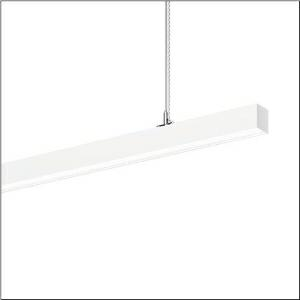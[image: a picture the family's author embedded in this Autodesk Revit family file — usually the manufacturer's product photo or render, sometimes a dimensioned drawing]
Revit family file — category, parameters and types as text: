
# Revit family: silica_r__21_51mx33tat7w_2751
name_source: partatom
category: Lighting Fixtures
units: mm (PartAtom-declared; Revit-internal decimal feet)

## family parameters
Cut with Voids When Loaded = No
Host = Face
Light Source = No
Part Type = Normal
Room Calculation Point = No
Round Connector Dimension = Use Diameter
Shared = No

## types (1)
- --- (1 x LED, 5740 lm, 53.8 W, 6500K)
    Apparent Load = 54 VA
    CIE Flux Codes = 78 96 99 56 100
    Color Rendering = 80
    Color Temperature = 6500K
    Default Elevation = 1800 mm
    Description = Silica® 21, office luminaire, primary optical cover: prismatic diffuser, of PMMA, CAT 2 (L<= 3000cd/m²), light emission: direct/indirect distribution, primary light characteristic: symmetric, installation type: suspended mounting, LED, rated luminous flux: 5.740lm, luminous efficacy: 102lm/W, light colour: 8tw, colour temperature: 2700..6500K, control gear: ECG DALI, with terminal, 3+2-pole, max. 2.5mm², mains connection: 220..240V, AC, 50/60Hz, rated input power: 56.5W, luminaire housing, of aluminium, traffic white (RAL 9016), length: 1.204mm, width: 53mm, height: 53mm, protection rating (complete): IP20, insulation class (complete): insulation class I (protective earthing), certification: CE, permissible operating ambient temperature: 0..+35°C, standard: EN 50419, packaging unit: 1 piece
    Height = 53 mm
    Lamp = 1 x LED
    Lamp Light Flux = 5740 lm
    Lamp Power = 53.8 W
    Lamp count = 1
    Length = 1204 mm
    Luminous efficacy = 107 lm/W
    Manufacturer = Siteco
    ModVariant = No
    Model = 51MX33TAT7W
    Mounting Place = Ceiling
    Mounting Type = Pendant
    Number of Poles = 1
    OnlyDefault = Yes
    Power Factor = 1
    Product Name = Silica® 21
    Product group = office luminaire | ceiling pendant
    ProductGroupID = 905
    Protection Class = Protection class I
    Protection Degree = IP 20
    RLX_Detail_Level = 1
    RlxData = <blob elided: 18217 chars, md5=e44a0a5e>
    Socket = socket
    Standby Power = 0 W
    System Light Flux = 5740 lm
    System Power = 54 W
    Type Comments = individual setting
    Type Image = l_1251642.jpg
    URL = http://relux.com
    VarID = @adj_045873
    Voltage = 0 V
    Weight = 0.00 kg
    Width = 53 mm

## geometry (parser evidence)
native form markers: Blend x4, Sweep x13
no freeform markers — native parametric forms only
